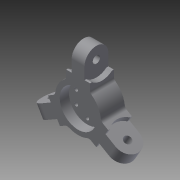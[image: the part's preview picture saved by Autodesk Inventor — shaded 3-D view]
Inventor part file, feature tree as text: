
AUTODESK INVENTOR PART (.ipt)
format: ipt  version: 2014 SP2 (Build 180246200, 246)  size: 227,328 bytes
history: native  units: mm
features: extrude x5, sketch x5, fillet x2, pattern_circular x2, mirror x1
ambient origin geometry x8: Origin, YZ Plane, XZ Plane, XY Plane, X Axis, Y Axis, Z Axis, Center Point
bodies: Solid1 (feature_tree)
feature tree (15):
  extrude  "Extrusion1"  TaperAngle=120.0deg  [1 undecoded]
  extrude  "Extrusion2"  Depth=26.0mm
  fillet  "Fillet1"  Radius=5.0mm
  extrude  "Extrusion3"  Depth=14.0mm
  mirror  "Mirror1"
  fillet  "Fillet2"  Radius=26.0mm
  pattern_circular  "Circular Pattern2"  [2 undecoded]
  extrude  "Extrusion4"  Depth=13.0mm
  pattern_circular  "Circular Pattern3"  [2 undecoded]
  extrude  "Extrusion6"  Depth=5.0mm
  sketch  "Sketch1"  dims[d0=50.0mm d1=120.0deg]
  sketch  "Sketch2"  dims[d2=120.0deg d3=26.0mm d4=5.0mm]
  sketch  "Sketch3"  dims[d5=30.0mm d6=14.0mm d7=26.0mm d8=0.0mm]
  sketch  "Sketch4"  dims[d12=8.0mm]
  sketch  "Sketch6"  dims[d13=13.0mm d14=15.0mm d15=0.0mm d16=13.0mm d17=15.0mm d18=0.0mm d19=5.0mm d20=30.0mm d21=360.0deg d23=28.0mm d24=4.0mm d25=15.0mm d26=0.0mm d30=60.0mm d31=360.0deg d33=40.0mm d34=10.0mm d35=0.0mm]
note: 5 required parameter values undecoded (feature->parameter linkage not recoverable at this tier; creation-order binding heuristic only, values carry confidence <= 0.55)
